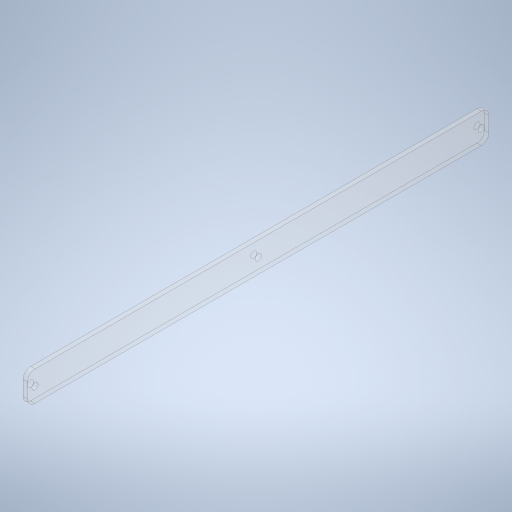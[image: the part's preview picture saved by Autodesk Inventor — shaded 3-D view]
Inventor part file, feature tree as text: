
AUTODESK INVENTOR PART (.ipt)
format: ipt  version: 2024 (Build 280153000, 153)  size: 271,872 bytes
history: native  units: mm
features: sketch x3, extrude x2, other x1, hole x1, fillet x1
ambient origin geometry x8: Origin, YZ Plane, XZ Plane, XY Plane, X Axis, Y Axis, Z Axis, Center Point
bodies: Body1 (feature_tree)
feature tree (8):
  other  "솔리드1"
  extrude  "돌출1"  Depth=20.0mm
  hole  "구멍1"  [1 undecoded]
  fillet  "모깎기1"  Radius=155.0mm
  extrude  "돌출2"  Depth=10.0mm
  sketch  "스케치1"
  sketch  "스케치2"
  sketch  "스케치3"
note: 1 required parameter value undecoded (feature->parameter linkage not recoverable at this tier; creation-order binding heuristic only, values carry confidence <= 0.55)
